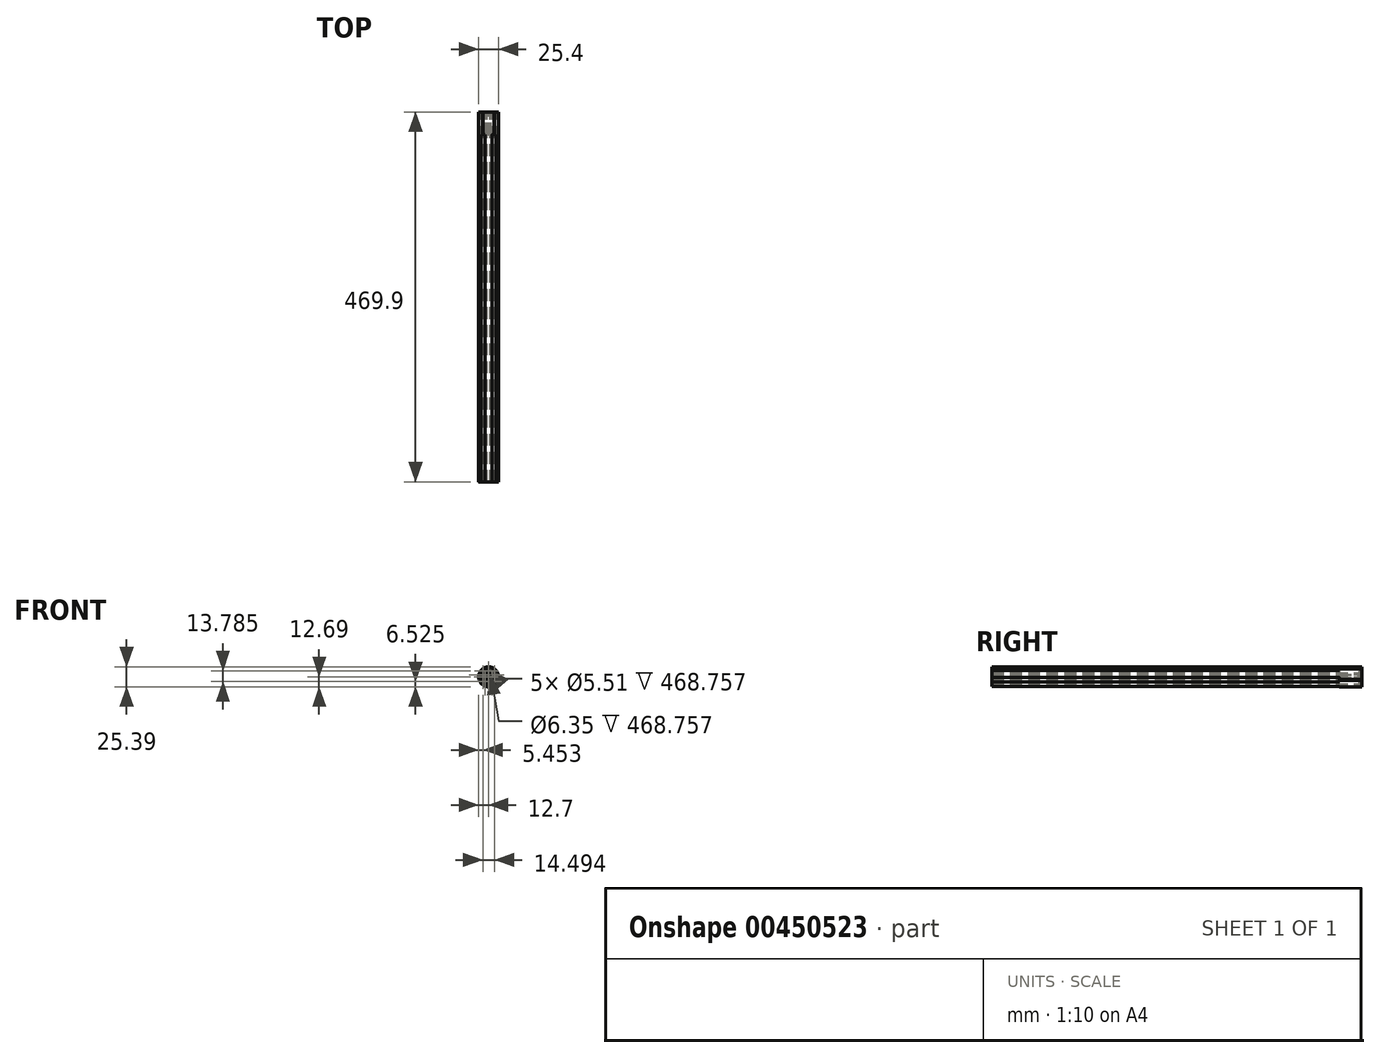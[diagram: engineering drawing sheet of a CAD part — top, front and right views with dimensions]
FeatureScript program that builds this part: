
annotation { "Feature Type Name" : "Feature", "Feature Type Description" : "" }
export const myFeature = defineFeature(function(context is Context, id is Id, definition is map)
    precondition{}
    {
        {
            var Q0;
            Q0=qCreatedBy(makeId("Front.planeOp"),FACE);
            var sketch = newSketch(context, id + "F0", { "sketchPlane" : qUnion([Q0])});
            skLineSegment(sketch, "E0", {"start": v(0, 0) * mm, "end": v(-7.46, 10.27) * mm});
            skLineSegment(sketch, "E1", {"start": v(0, 0) * mm, "end": v(7.46, 10.27) * mm});
            skArc(sketch, "E2", {"start": v(7.46, 10.27) * mm, "mid": v(0, 12.7) * mm, "end": v(-7.46, 10.27) * mm});
            skCircle(sketch, "E3", {"center": v(0, 7.62) * mm, "radius": 3.97 * mm});
            skCircle(sketch, "E4", {"center": v(0, 7.62) * mm, "radius": 3.66 * mm});
            skCircle(sketch, "E5", {"center": v(0, 7.62) * mm, "radius": 2.76 * mm});
            skLineSegment(sketch, "E6", {"start": v(3.41, 5.37) * mm, "end": v(7.14, 10.5) * mm});
            skLineSegment(sketch, "E7", {"start": v(3.41, 5.37) * mm, "end": v(0, 0.68) * mm});
            skLineSegment(sketch, "E8", {"start": v(-3.41, 5.37) * mm, "end": v(-7.14, 10.5) * mm});
            skLineSegment(sketch, "E9", {"start": v(-3.41, 5.37) * mm, "end": v(0, 0.68) * mm});
            skLineSegment(sketch, "E10", {"start": v(0, 3.17) * mm, "end": v(2.3, 3.17) * mm});
            skLineSegment(sketch, "E11", {"start": v(0, 3.17) * mm, "end": v(-2.3, 3.17) * mm});
            skLineSegment(sketch, "E12", {"start": v(0, 11.28) * mm, "end": v(5.84, 11.28) * mm});
            skLineSegment(sketch, "E13", {"start": v(0, 11.28) * mm, "end": v(-5.84, 11.28) * mm});
            skPoint(sketch, "E14.orphan", {"position": v(0, 12.7) * mm});
            skArc(sketch, "E15", {"start": v(1.87, 2.57) * mm, "mid": v(0, 3.17) * mm, "end": v(-1.87, 2.57) * mm});
            skArc(sketch, "E16", {"start": v(-5.6, 7.7) * mm, "mid": v(-4.37, 9.58) * mm, "end": v(-4.68, 11.8) * mm});
            skArc(sketch, "E17", {"start": v(4.68, 11.8) * mm, "mid": v(4.37, 9.58) * mm, "end": v(5.6, 7.7) * mm});
            skLineSegment(sketch, "E18", {"start": v(0, 7.62) * mm, "end": v(-5.54, 7.62) * mm});
            skLineSegment(sketch, "E19", {"start": v(0, 7.62) * mm, "end": v(5.54, 7.62) * mm});
            skLineSegment(sketch, "E20", {"start": v(1.82, 3.17) * mm, "end": v(1.82, 4.45) * mm});
            skLineSegment(sketch, "E21", {"start": v(-1.82, 3.17) * mm, "end": v(-1.82, 4.45) * mm});
            skLineSegment(sketch, "E22", {"start": v(1.82, 4.45) * mm, "end": v(1.82, 5.55) * mm});
            skLineSegment(sketch, "E23", {"start": v(-1.82, 4.45) * mm, "end": v(-1.82, 5.55) * mm});
            skSolve(sketch);
        }
        {
            var Q0;
            {var subQ3=sQuery(id+"F0.wireOp",EDGE,"E11");var subQ7=sQuery(id+"F0.wireOp",EDGE,"E0");var subQ8=makeQuery(id+"F0.imprint","INTERSECT",VERTEX,{"derivedFrom":[subQ7,subQ3]});Q0=makeQuery(id+"F0.imprint","IMPRINT",FACE,{"disambiguationData":[TD([[makeQuery(id+"F0.imprint","IMPRINT",EDGE,{"disambiguationData":[TD([[subQ8,-1.0]])],"derivedFrom":subQ7}),-1.0]])]});}
            var Q1;
            {var subQ0=sQuery(id+"F0.wireOp",EDGE,"E11");var subQ1=sQuery(id+"F0.wireOp",EDGE,"E0");var subQ2=makeQuery(id+"F0.imprint","INTERSECT",VERTEX,{"derivedFrom":[subQ1,subQ0]});Q1=makeQuery(id+"F0.imprint","IMPRINT",FACE,{"disambiguationData":[TD([[makeQuery(id+"F0.imprint","IMPRINT",EDGE,{"disambiguationData":[TD([[subQ2,1.0]])],"derivedFrom":subQ1}),-1.0]])]});}
            var Q2;
            {var subQ0=sQuery(id+"F0.wireOp",EDGE,"E11");var subQ1=sQuery(id+"F0.wireOp",EDGE,"E9");var subQ2=makeQuery(id+"F0.imprint","INTERSECT",VERTEX,{"derivedFrom":[subQ1,subQ0]});Q2=makeQuery(id+"F0.imprint","IMPRINT",FACE,{"disambiguationData":[TD([[makeQuery(id+"F0.imprint","IMPRINT",EDGE,{"disambiguationData":[TD([[subQ2,-1.0]])],"derivedFrom":subQ1}),1.0]])]});}
            var Q3;
            {var subQ3=sQuery(id+"F0.wireOp",EDGE,"E16");var subQ9=sQuery(id+"F0.wireOp",EDGE,"E2");var subQ10=makeQuery(id+"F0.imprint","INTERSECT",VERTEX,{"derivedFrom":[subQ9,subQ3]});Q3=makeQuery(id+"F0.imprint","IMPRINT",FACE,{"disambiguationData":[TD([[makeQuery(id+"F0.imprint","IMPRINT",EDGE,{"disambiguationData":[TD([[subQ10,1.0]])],"derivedFrom":subQ9}),1.0]])]});}
            var Q4;
            {var subQ0=sQuery(id+"F0.wireOp",EDGE,"E12");var subQ1=sQuery(id+"F0.wireOp",EDGE,"E3");var subQ2=makeQuery(id+"F0.imprint","INTERSECT",VERTEX,{"derivedFrom":[subQ1,subQ0]});Q4=makeQuery(id+"F0.imprint","IMPRINT",FACE,{"disambiguationData":[TD([[makeQuery(id+"F0.imprint","IMPRINT",EDGE,{"disambiguationData":[TD([[subQ2,-1.0]])],"derivedFrom":subQ1}),1.0]])]});}
            var Q5;
            {var subQ10=sQuery(id+"F0.wireOp",EDGE,"E12");var subQ11=sQuery(id+"F0.wireOp",EDGE,"E3");var subQ12=makeQuery(id+"F0.imprint","INTERSECT",VERTEX,{"derivedFrom":[subQ11,subQ10]});Q5=makeQuery(id+"F0.imprint","IMPRINT",FACE,{"disambiguationData":[TD([[makeQuery(id+"F0.imprint","IMPRINT",EDGE,{"disambiguationData":[TD([[subQ12,1.0]])],"derivedFrom":subQ11}),-1.0]])]});}
            var Q6;
            {var subQ5=sQuery(id+"F0.wireOp",EDGE,"E4");Q6=makeQuery(id+"F0.imprint","IMPRINT",FACE,{"disambiguationData":[TD([[makeQuery(id+"F0.imprint","IMPRINT",EDGE,{"derivedFrom":subQ5}),-1.0]])]});}
            var Q7;
            Q7=makeQuery(id+"F0.imprint","IMPRINT",FACE,{"disambiguationData":[TD([[makeQuery(id+"F0.imprint","IMPRINT",EDGE,{"derivedFrom":sQuery(id+"F0.wireOp",EDGE,"E4")}),1.0]])]});
            var Q8;
            {var subQ0=sQuery(id+"F0.wireOp",EDGE,"E10");var subQ1=sQuery(id+"F0.wireOp",EDGE,"E1");var subQ2=makeQuery(id+"F0.imprint","INTERSECT",VERTEX,{"derivedFrom":[subQ1,subQ0]});Q8=makeQuery(id+"F0.imprint","IMPRINT",FACE,{"disambiguationData":[TD([[makeQuery(id+"F0.imprint","IMPRINT",EDGE,{"disambiguationData":[TD([[subQ2,-1.0]])],"derivedFrom":subQ1}),1.0]])]});}
            var Q9;
            {var subQ0=sQuery(id+"F0.wireOp",EDGE,"E10");var subQ1=sQuery(id+"F0.wireOp",EDGE,"E7");var subQ2=makeQuery(id+"F0.imprint","INTERSECT",VERTEX,{"derivedFrom":[subQ1,subQ0]});Q9=makeQuery(id+"F0.imprint","IMPRINT",FACE,{"disambiguationData":[TD([[makeQuery(id+"F0.imprint","IMPRINT",EDGE,{"disambiguationData":[TD([[subQ2,-1.0]])],"derivedFrom":subQ1}),-1.0]])]});}
            var Q10;
            {var subQ0=sQuery(id+"F0.wireOp",EDGE,"E10");var subQ1=sQuery(id+"F0.wireOp",EDGE,"E1");var subQ2=makeQuery(id+"F0.imprint","INTERSECT",VERTEX,{"derivedFrom":[subQ1,subQ0]});Q10=makeQuery(id+"F0.imprint","IMPRINT",FACE,{"disambiguationData":[TD([[makeQuery(id+"F0.imprint","IMPRINT",EDGE,{"disambiguationData":[TD([[subQ2,1.0]])],"derivedFrom":subQ1}),1.0]])]});}
            var Q11;
            {var subQ13=sQuery(id+"F0.wireOp",EDGE,"E19");var subQ15=sQuery(id+"F0.wireOp",EDGE,"E3");var subQ16=makeQuery(id+"F0.imprint","INTERSECT",VERTEX,{"derivedFrom":[subQ15,subQ13]});Q11=makeQuery(id+"F0.imprint","IMPRINT",FACE,{"disambiguationData":[TD([[makeQuery(id+"F0.imprint","IMPRINT",EDGE,{"disambiguationData":[TD([[subQ16,1.0]])],"derivedFrom":subQ15}),-1.0]])]});}
            var Q12;
            {var subQ0=sQuery(id+"F0.wireOp",EDGE,"E13");var subQ1=sQuery(id+"F0.wireOp",EDGE,"E3");var subQ2=makeQuery(id+"F0.imprint","INTERSECT",VERTEX,{"derivedFrom":[subQ1,subQ0]});Q12=makeQuery(id+"F0.imprint","IMPRINT",FACE,{"disambiguationData":[TD([[makeQuery(id+"F0.imprint","IMPRINT",EDGE,{"disambiguationData":[TD([[subQ2,-1.0]])],"derivedFrom":subQ1}),-1.0]])]});}
            var Q13;
            {var subQ0=sQuery(id+"F0.wireOp",EDGE,"E16");var subQ1=sQuery(id+"F0.wireOp",EDGE,"E0");var subQ2=makeQuery(id+"F0.imprint","INTERSECT",VERTEX,{"derivedFrom":[subQ1,subQ0]});Q13=makeQuery(id+"F0.imprint","IMPRINT",FACE,{"disambiguationData":[TD([[makeQuery(id+"F0.imprint","IMPRINT",EDGE,{"disambiguationData":[TD([[subQ2,1.0]])],"derivedFrom":subQ1}),-1.0]])]});}
            var Q14;
            {var subQ0=sQuery(id+"F0.wireOp",EDGE,"E17");var subQ1=sQuery(id+"F0.wireOp",EDGE,"E1");var subQ2=makeQuery(id+"F0.imprint","INTERSECT",VERTEX,{"derivedFrom":[subQ1,subQ0]});Q14=makeQuery(id+"F0.imprint","IMPRINT",FACE,{"disambiguationData":[TD([[makeQuery(id+"F0.imprint","IMPRINT",EDGE,{"disambiguationData":[TD([[subQ2,1.0]])],"derivedFrom":subQ1}),1.0]])]});}
            var Q15;
            {var subQ0=sQuery(id+"F0.wireOp",EDGE,"E19");var subQ1=sQuery(id+"F0.wireOp",EDGE,"E4");var subQ2=makeQuery(id+"F0.imprint","INTERSECT",VERTEX,{"derivedFrom":[subQ1,subQ0]});Q15=makeQuery(id+"F0.imprint","IMPRINT",FACE,{"disambiguationData":[TD([[makeQuery(id+"F0.imprint","IMPRINT",EDGE,{"disambiguationData":[TD([[subQ2,1.0]])],"derivedFrom":subQ1}),1.0]])]});}
            var Q16;
            {var subQ0=sQuery(id+"F0.wireOp",EDGE,"VKm7TL3z-6OuM-YeBj-8OZN-xYRqr5il45Gy");var subQ1=sQuery(id+"F0.wireOp",EDGE,"E4");var subQ2=makeQuery(id+"F0.imprint","INTERSECT",VERTEX,{"derivedFrom":[subQ1,subQ0]});Q16=makeQuery(id+"F0.imprint","IMPRINT",FACE,{"disambiguationData":[TD([[makeQuery(id+"F0.imprint","IMPRINT",EDGE,{"disambiguationData":[TD([[subQ2,-1.0]])],"derivedFrom":subQ1}),1.0]])]});}
            var Q17;
            {var subQ0=sQuery(id+"F0.wireOp",EDGE,"E18");var subQ1=sQuery(id+"F0.wireOp",EDGE,"E4");var subQ2=makeQuery(id+"F0.imprint","INTERSECT",VERTEX,{"derivedFrom":[subQ1,subQ0]});Q17=makeQuery(id+"F0.imprint","IMPRINT",FACE,{"disambiguationData":[TD([[makeQuery(id+"F0.imprint","IMPRINT",EDGE,{"disambiguationData":[TD([[subQ2,-1.0]])],"derivedFrom":subQ1}),1.0]])]});}
            var Q18;
            {var subQ0=sQuery(id+"F0.wireOp",EDGE,"E18");var subQ1=sQuery(id+"F0.wireOp",EDGE,"E3");var subQ2=makeQuery(id+"F0.imprint","INTERSECT",VERTEX,{"derivedFrom":[subQ1,subQ0]});Q18=makeQuery(id+"F0.imprint","IMPRINT",FACE,{"disambiguationData":[TD([[makeQuery(id+"F0.imprint","IMPRINT",EDGE,{"disambiguationData":[TD([[subQ2,-1.0]])],"derivedFrom":subQ1}),-1.0]])]});}
            var Q19;
            {var subQ0=sQuery(id+"F0.wireOp",EDGE,"VKm7TL3z-6OuM-YeBj-8OZN-xYRqr5il45Gy");var subQ5=sQuery(id+"F0.wireOp",EDGE,"E3");var subQ6=makeQuery(id+"F0.imprint","INTERSECT",VERTEX,{"derivedFrom":[subQ5,subQ0]});Q19=makeQuery(id+"F0.imprint","IMPRINT",FACE,{"disambiguationData":[TD([[makeQuery(id+"F0.imprint","IMPRINT",EDGE,{"disambiguationData":[TD([[subQ6,-1.0]])],"derivedFrom":subQ5}),-1.0]])]});}
            var Q20;
            {var subQ0=sQuery(id+"F0.wireOp",EDGE,"E11");var subQ1=sQuery(id+"F0.wireOp",EDGE,"E9");var subQ2=makeQuery(id+"F0.imprint","INTERSECT",VERTEX,{"derivedFrom":[subQ1,subQ0]});Q20=makeQuery(id+"F0.imprint","IMPRINT",FACE,{"disambiguationData":[TD([[makeQuery(id+"F0.imprint","IMPRINT",EDGE,{"disambiguationData":[TD([[subQ2,-1.0]])],"derivedFrom":subQ1}),-1.0]])]});}
            var Q21;
            {var subQ0=sQuery(id+"F0.wireOp",EDGE,"E10");var subQ1=sQuery(id+"F0.wireOp",EDGE,"E7");var subQ2=makeQuery(id+"F0.imprint","INTERSECT",VERTEX,{"derivedFrom":[subQ1,subQ0]});Q21=makeQuery(id+"F0.imprint","IMPRINT",FACE,{"disambiguationData":[TD([[makeQuery(id+"F0.imprint","IMPRINT",EDGE,{"disambiguationData":[TD([[subQ2,-1.0]])],"derivedFrom":subQ1}),1.0]])]});}
            var Q22;
            {var subQ0=sQuery(id+"F0.wireOp",EDGE,"Kxilka5q-FxSn-3UiT-ll3h-Z3imloTSvPit");var subQ1=sQuery(id+"F0.wireOp",EDGE,"E7");var subQ2=makeQuery(id+"F0.imprint","INTERSECT",VERTEX,{"derivedFrom":[subQ1,subQ0]});Q22=makeQuery(id+"F0.imprint","IMPRINT",FACE,{"disambiguationData":[TD([[makeQuery(id+"F0.imprint","IMPRINT",EDGE,{"disambiguationData":[TD([[subQ2,-1.0]])],"derivedFrom":subQ1}),1.0]])]});}
            var Q23;
            {var subQ0=sQuery(id+"F0.wireOp",EDGE,"VKm7TL3z-6OuM-YeBj-8OZN-xYRqr5il45Gy");var subQ1=sQuery(id+"F0.wireOp",EDGE,"E9");var subQ2=makeQuery(id+"F0.imprint","INTERSECT",VERTEX,{"derivedFrom":[subQ1,subQ0]});Q23=makeQuery(id+"F0.imprint","IMPRINT",FACE,{"disambiguationData":[TD([[makeQuery(id+"F0.imprint","IMPRINT",EDGE,{"disambiguationData":[TD([[subQ2,-1.0]])],"derivedFrom":subQ1}),-1.0]])]});}
            var Q24;
            {var subQ2=sQuery(id+"F0.wireOp",EDGE,"E18");var subQ6=sQuery(id+"F0.wireOp",EDGE,"E5");var subQ8=makeQuery(id+"F0.imprint","INTERSECT",VERTEX,{"derivedFrom":[subQ6,subQ2]});Q24=makeQuery(id+"F0.imprint","IMPRINT",FACE,{"disambiguationData":[TD([[makeQuery(id+"F0.imprint","IMPRINT",EDGE,{"disambiguationData":[TD([[subQ8,1.0]])],"derivedFrom":subQ6}),-1.0]])]});}
            var Q25;
            {var subQ0=sQuery(id+"F0.wireOp",EDGE,"E22");Q25=makeQuery(id+"F0.imprint","IMPRINT",FACE,{"disambiguationData":[TD([[makeQuery(id+"F0.imprint","IMPRINT",EDGE,{"derivedFrom":subQ0}),1.0]])]});}
            extrude(context, id + "F1", {"entities" : qUnion([Q0, Q1, Q2, Q3, Q4, Q5, Q6, Q7, Q8, Q9, Q10, Q11, Q12, Q13, Q14, Q15, Q16, Q17, Q18, Q19, Q20, Q21, Q22, Q23, Q24, Q25]), "depth" : 469.9 * mm});
        }
        {
            var Q0;
            Q0=qCreatedBy(makeId("Top.planeOp"),FACE);
            var sketch = newSketch(context, id + "F2", { "sketchPlane" : qUnion([Q0])});
            skLineSegment(sketch, "E24", {"start": v(0, 0) * mm, "end": v(0, -12.7) * mm});
            skSolve(sketch);
        }
        {
            var Q0;
            {var subQ0=sQuery(id+"F0.wireOp",EDGE,"E22");Q0=makeQuery(id+"F0.imprint","IMPRINT",FACE,{"disambiguationData":[TD([[makeQuery(id+"F0.imprint","IMPRINT",EDGE,{"derivedFrom":subQ0}),-1.0]])]});}
            var Q1;
            {var subQ5=sQuery(id+"F0.wireOp",EDGE,"E19");var subQ6=sQuery(id+"F0.wireOp",EDGE,"E3");var subQ7=makeQuery(id+"F0.imprint","INTERSECT",VERTEX,{"derivedFrom":[subQ6,subQ5]});Q1=makeQuery(id+"F0.imprint","IMPRINT",FACE,{"disambiguationData":[TD([[makeQuery(id+"F0.imprint","IMPRINT",EDGE,{"disambiguationData":[TD([[subQ7,1.0]])],"derivedFrom":subQ6}),-1.0]])]});}
            var Q2;
            {var subQ0=sQuery(id+"F0.wireOp",EDGE,"E19");var subQ1=sQuery(id+"F0.wireOp",EDGE,"E3");var subQ2=makeQuery(id+"F0.imprint","INTERSECT",VERTEX,{"derivedFrom":[subQ1,subQ0]});Q2=makeQuery(id+"F0.imprint","IMPRINT",FACE,{"disambiguationData":[TD([[makeQuery(id+"F0.imprint","IMPRINT",EDGE,{"disambiguationData":[TD([[subQ2,1.0]])],"derivedFrom":subQ1}),1.0]])]});}
            var Q3;
            {var subQ0=sQuery(id+"F0.wireOp",EDGE,"E23");Q3=makeQuery(id+"F0.imprint","IMPRINT",FACE,{"disambiguationData":[TD([[makeQuery(id+"F0.imprint","IMPRINT",EDGE,{"derivedFrom":subQ0}),1.0]])]});}
            var Q4;
            {var subQ0=sQuery(id+"F0.wireOp",EDGE,"E18");var subQ1=sQuery(id+"F0.wireOp",EDGE,"E3");var subQ2=makeQuery(id+"F0.imprint","INTERSECT",VERTEX,{"derivedFrom":[subQ1,subQ0]});Q4=makeQuery(id+"F0.imprint","IMPRINT",FACE,{"disambiguationData":[TD([[makeQuery(id+"F0.imprint","IMPRINT",EDGE,{"disambiguationData":[TD([[subQ2,-1.0]])],"derivedFrom":subQ1}),1.0]])]});}
            var Q5;
            {var subQ0=sQuery(id+"F0.wireOp",EDGE,"E18");var subQ1=sQuery(id+"F0.wireOp",EDGE,"E3");var subQ2=makeQuery(id+"F0.imprint","INTERSECT",VERTEX,{"derivedFrom":[subQ1,subQ0]});Q5=makeQuery(id+"F0.imprint","IMPRINT",FACE,{"disambiguationData":[TD([[makeQuery(id+"F0.imprint","IMPRINT",EDGE,{"disambiguationData":[TD([[subQ2,-1.0]])],"derivedFrom":subQ1}),-1.0]])]});}
            extrude(context, id + "F3", {"entities" : qUnion([Q0, Q1, Q2, Q3, Q4, Q5]), "operationType" : NewBodyOperationType.REMOVE, "depth" : 3.17 * mm});
        }
        {
            var Q0;
            {var subQ0=sQuery(id+"F0.wireOp",EDGE,"E17");var subQ1=sQuery(id+"F0.wireOp",EDGE,"E1");var subQ2=makeQuery(id+"F0.imprint","INTERSECT",VERTEX,{"derivedFrom":[subQ1,subQ0]});Q0=makeQuery(id+"F0.imprint","IMPRINT",FACE,{"disambiguationData":[TD([[makeQuery(id+"F0.imprint","IMPRINT",EDGE,{"disambiguationData":[TD([[subQ2,1.0]])],"derivedFrom":subQ1}),1.0]])]});}
            var Q1;
            {var subQ0=sQuery(id+"F0.wireOp",EDGE,"E10");var subQ1=sQuery(id+"F0.wireOp",EDGE,"E1");var subQ2=makeQuery(id+"F0.imprint","INTERSECT",VERTEX,{"derivedFrom":[subQ1,subQ0]});Q1=makeQuery(id+"F0.imprint","IMPRINT",FACE,{"disambiguationData":[TD([[makeQuery(id+"F0.imprint","IMPRINT",EDGE,{"disambiguationData":[TD([[subQ2,-1.0]])],"derivedFrom":subQ1}),1.0]])]});}
            var Q2;
            {var subQ0=sQuery(id+"F0.wireOp",EDGE,"E10");var subQ1=sQuery(id+"F0.wireOp",EDGE,"E1");var subQ2=makeQuery(id+"F0.imprint","INTERSECT",VERTEX,{"derivedFrom":[subQ1,subQ0]});Q2=makeQuery(id+"F0.imprint","IMPRINT",FACE,{"disambiguationData":[TD([[makeQuery(id+"F0.imprint","IMPRINT",EDGE,{"disambiguationData":[TD([[subQ2,1.0]])],"derivedFrom":subQ1}),1.0]])]});}
            var Q3;
            {var subQ0=sQuery(id+"F0.wireOp",EDGE,"E11");var subQ1=sQuery(id+"F0.wireOp",EDGE,"E0");var subQ2=makeQuery(id+"F0.imprint","INTERSECT",VERTEX,{"derivedFrom":[subQ1,subQ0]});Q3=makeQuery(id+"F0.imprint","IMPRINT",FACE,{"disambiguationData":[TD([[makeQuery(id+"F0.imprint","IMPRINT",EDGE,{"disambiguationData":[TD([[subQ2,1.0]])],"derivedFrom":subQ1}),-1.0]])]});}
            var Q4;
            {var subQ3=sQuery(id+"F0.wireOp",EDGE,"E11");var subQ7=sQuery(id+"F0.wireOp",EDGE,"E0");var subQ8=makeQuery(id+"F0.imprint","INTERSECT",VERTEX,{"derivedFrom":[subQ7,subQ3]});Q4=makeQuery(id+"F0.imprint","IMPRINT",FACE,{"disambiguationData":[TD([[makeQuery(id+"F0.imprint","IMPRINT",EDGE,{"disambiguationData":[TD([[subQ8,-1.0]])],"derivedFrom":subQ7}),-1.0]])]});}
            var Q5;
            {var subQ0=sQuery(id+"F0.wireOp",EDGE,"E16");var subQ1=sQuery(id+"F0.wireOp",EDGE,"E0");var subQ2=makeQuery(id+"F0.imprint","INTERSECT",VERTEX,{"derivedFrom":[subQ1,subQ0]});Q5=makeQuery(id+"F0.imprint","IMPRINT",FACE,{"disambiguationData":[TD([[makeQuery(id+"F0.imprint","IMPRINT",EDGE,{"disambiguationData":[TD([[subQ2,1.0]])],"derivedFrom":subQ1}),-1.0]])]});}
            extrude(context, id + "F4", {"entities" : qUnion([Q0, Q1, Q2, Q3, Q4, Q5]), "operationType" : NewBodyOperationType.REMOVE, "depth" : 28.57 * mm});
        }
        {
            var Q0;
            {var subQ0=sQuery(id+"F0.wireOp",EDGE,"E18");var subQ3=sQuery(id+"F0.wireOp",EDGE,"E5");var subQ4=makeQuery(id+"F0.imprint","INTERSECT",VERTEX,{"derivedFrom":[subQ3,subQ0]});Q0=makeQuery(id+"F0.imprint","IMPRINT",FACE,{"disambiguationData":[TD([[makeQuery(id+"F0.imprint","IMPRINT",EDGE,{"disambiguationData":[TD([[subQ4,1.0]])],"derivedFrom":subQ3}),-1.0]])]});}
            var Q1;
            {var subQ0=sQuery(id+"F0.wireOp",EDGE,"E21");var subQ1=sQuery(id+"F0.wireOp",EDGE,"E3");var subQ2=makeQuery(id+"F0.imprint","INTERSECT",VERTEX,{"derivedFrom":[subQ1,subQ0]});Q1=makeQuery(id+"F0.imprint","IMPRINT",FACE,{"disambiguationData":[TD([[makeQuery(id+"F0.imprint","IMPRINT",EDGE,{"disambiguationData":[TD([[subQ2,-1.0]])],"derivedFrom":subQ1}),1.0]])]});}
            var Q2;
            {var subQ3=sQuery(id+"F0.wireOp",EDGE,"E3");var subQ7=sQuery(id+"F0.wireOp",EDGE,"E21");var subQ9=makeQuery(id+"F0.imprint","INTERSECT",VERTEX,{"derivedFrom":[subQ3,subQ7]});Q2=makeQuery(id+"F0.imprint","IMPRINT",FACE,{"disambiguationData":[TD([[makeQuery(id+"F0.imprint","IMPRINT",EDGE,{"disambiguationData":[TD([[subQ9,-1.0]])],"derivedFrom":subQ3}),-1.0]])]});}
            var Q3;
            {var subQ1=sQuery(id+"F0.wireOp",EDGE,"E7");var subQ3=sQuery(id+"F0.wireOp",EDGE,"E15");var subQ4=makeQuery(id+"F0.imprint","INTERSECT",VERTEX,{"derivedFrom":[subQ1,subQ3]});Q3=makeQuery(id+"F0.imprint","IMPRINT",FACE,{"disambiguationData":[TD([[makeQuery(id+"F0.imprint","IMPRINT",EDGE,{"disambiguationData":[TD([[subQ4,1.0]])],"derivedFrom":subQ1}),-1.0]])]});}
            var Q4;
            {var subQ1=sQuery(id+"F0.wireOp",EDGE,"E9");var subQ3=sQuery(id+"F0.wireOp",EDGE,"E15");var subQ4=makeQuery(id+"F0.imprint","INTERSECT",VERTEX,{"derivedFrom":[subQ1,subQ3]});Q4=makeQuery(id+"F0.imprint","IMPRINT",FACE,{"disambiguationData":[TD([[makeQuery(id+"F0.imprint","IMPRINT",EDGE,{"disambiguationData":[TD([[subQ4,1.0]])],"derivedFrom":subQ1}),1.0]])]});}
            var Q5;
            {var subQ0=sQuery(id+"F0.wireOp",EDGE,"E22");Q5=makeQuery(id+"F0.imprint","IMPRINT",FACE,{"disambiguationData":[TD([[makeQuery(id+"F0.imprint","IMPRINT",EDGE,{"derivedFrom":subQ0}),1.0]])]});}
            extrude(context, id + "F5", {"entities" : qUnion([Q0, Q1, Q2, Q3, Q4, Q5]), "operationType" : NewBodyOperationType.REMOVE, "depth" : 1.14 * mm});
        }
        {
            var Q0;
            {var subQ0=sQuery(id+"F0.wireOp",EDGE,"E6");var subQ1=sQuery(id+"F0.wireOp",EDGE,"E2");var subQ2=makeQuery(id+"F0.imprint","INTERSECT",VERTEX,{"derivedFrom":[subQ1,subQ0]});Q0=makeQuery(id+"F0.imprint","IMPRINT",FACE,{"disambiguationData":[TD([[makeQuery(id+"F0.imprint","IMPRINT",EDGE,{"disambiguationData":[TD([[subQ2,-1.0]])],"derivedFrom":subQ1}),1.0]])]});}
            var Q1;
            {var subQ0=sQuery(id+"F0.wireOp",EDGE,"E12");var subQ1=sQuery(id+"F0.wireOp",EDGE,"E2");var subQ2=makeQuery(id+"F0.imprint","INTERSECT",VERTEX,{"derivedFrom":[subQ1,subQ0]});Q1=makeQuery(id+"F0.imprint","IMPRINT",FACE,{"disambiguationData":[TD([[makeQuery(id+"F0.imprint","IMPRINT",EDGE,{"disambiguationData":[TD([[subQ2,-1.0]])],"derivedFrom":subQ1}),1.0]])]});}
            var Q2;
            {var subQ0=sQuery(id+"F0.wireOp",EDGE,"E13");var subQ1=sQuery(id+"F0.wireOp",EDGE,"E2");var subQ2=makeQuery(id+"F0.imprint","INTERSECT",VERTEX,{"derivedFrom":[subQ1,subQ0]});Q2=makeQuery(id+"F0.imprint","IMPRINT",FACE,{"disambiguationData":[TD([[makeQuery(id+"F0.imprint","IMPRINT",EDGE,{"disambiguationData":[TD([[subQ2,1.0]])],"derivedFrom":subQ1}),1.0]])]});}
            var Q3;
            {var subQ0=sQuery(id+"F0.wireOp",EDGE,"E8");var subQ1=sQuery(id+"F0.wireOp",EDGE,"E2");var subQ2=makeQuery(id+"F0.imprint","INTERSECT",VERTEX,{"derivedFrom":[subQ1,subQ0]});Q3=makeQuery(id+"F0.imprint","IMPRINT",FACE,{"disambiguationData":[TD([[makeQuery(id+"F0.imprint","IMPRINT",EDGE,{"disambiguationData":[TD([[subQ2,1.0]])],"derivedFrom":subQ1}),1.0]])]});}
            extrude(context, id + "F6", {"entities" : qUnion([Q0, Q1, Q2, Q3]), "operationType" : NewBodyOperationType.ADD, "depth" : 28.57 * mm});
        }
        {
            var Q0;
            Q0=makeQuery(id+"F1.opExtrude","SWEPT_BODY",BODY,{"disambiguationData":[OSD([sQuery(id+"F0.wireOp",EDGE,"E0"),sQuery(id+"F0.wireOp",EDGE,"E1"),sQuery(id+"F0.wireOp",EDGE,"E2"),sQuery(id+"F0.wireOp",EDGE,"E5"),sQuery(id+"F0.wireOp",EDGE,"E15"),sQuery(id+"F0.wireOp",EDGE,"E16"),sQuery(id+"F0.wireOp",EDGE,"E17")])]});
            var Q1;
            Q1=sQuery(id+"F2.wireOp",EDGE,"E24");
            circularPattern(context, id + "F7", {"operationType" : NewBodyOperationType.ADD, "entities" : qUnion([Q0]), "axis" : qUnion([Q1]), "angle" : 360 * degree, "instanceCount" : 5, "equalSpace" : true, "computeTransformsWithoutBuiltin" : true});
        }
    });
